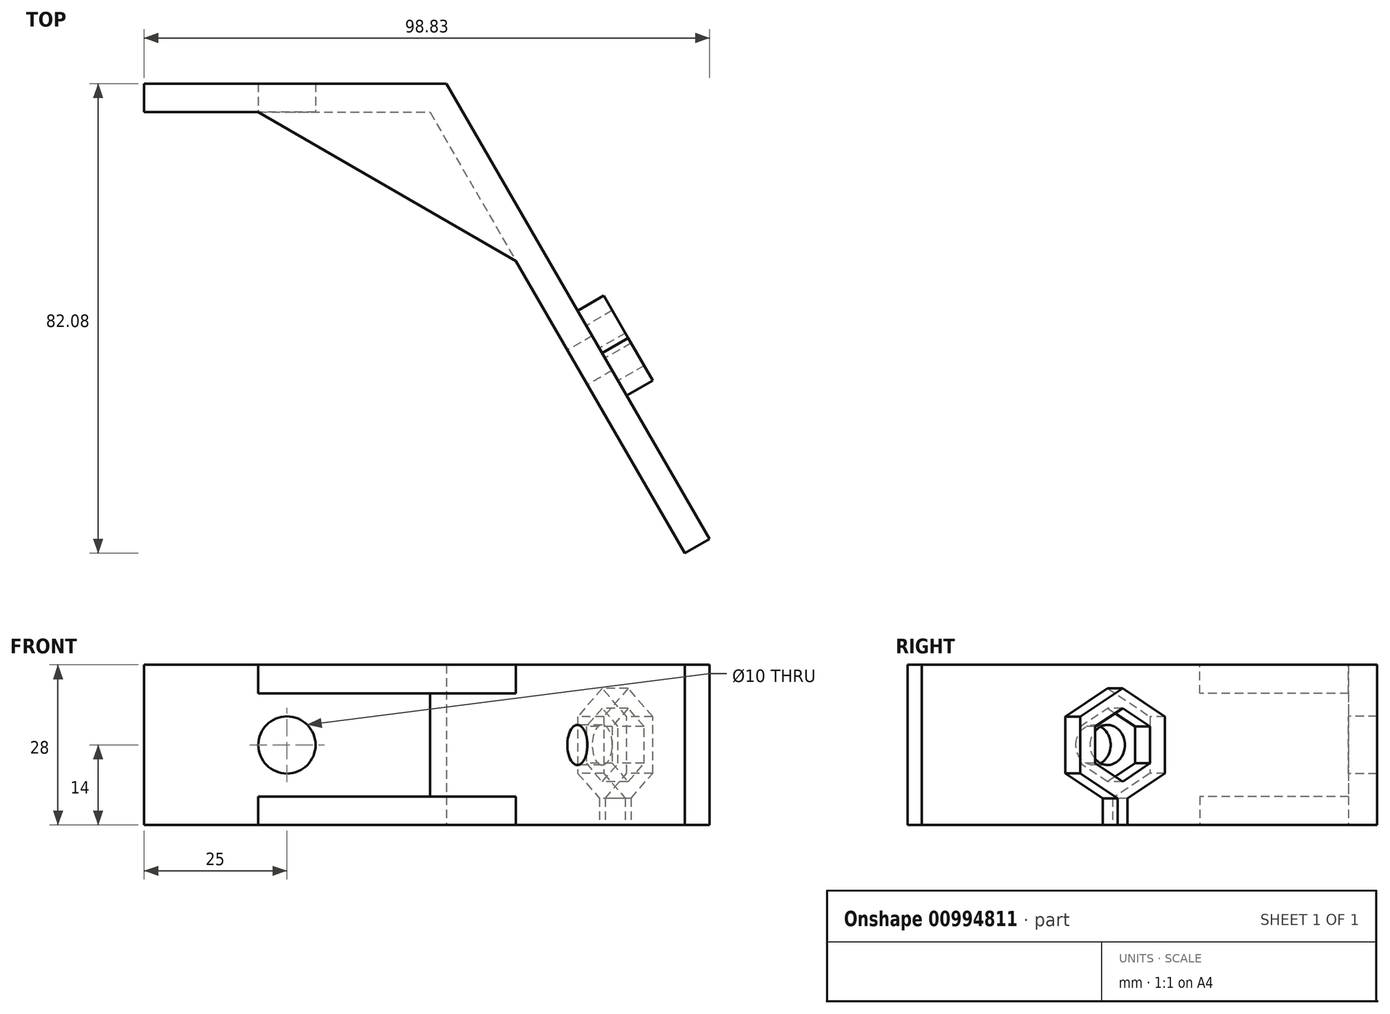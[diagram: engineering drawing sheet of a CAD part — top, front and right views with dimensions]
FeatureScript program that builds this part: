
annotation { "Feature Type Name" : "Feature", "Feature Type Description" : "" }
export const myFeature = defineFeature(function(context is Context, id is Id, definition is map)
    precondition{}
    {
        {
            var Q0;
            Q0=qCreatedBy(makeId("Top.planeOp"),FACE);
            var sketch = newSketch(context, id + "F0", { "sketchPlane" : qUnion([Q0])});
            skLineSegment(sketch, "E0", {"start": v(0, 5) * mm, "end": v(0, 0) * mm});
            skLineSegment(sketch, "E1", {"start": v(0, 0) * mm, "end": v(50, 0) * mm});
            skLineSegment(sketch, "E2", {"start": v(50, 0) * mm, "end": v(94.5, -77.08) * mm});
            skLineSegment(sketch, "E3", {"start": v(94.5, -77.08) * mm, "end": v(98.83, -74.58) * mm});
            skLineSegment(sketch, "E4", {"start": v(98.83, -74.58) * mm, "end": v(52.89, 5) * mm});
            skLineSegment(sketch, "E5", {"start": v(52.89, 5) * mm, "end": v(0, 5) * mm});
            skSolve(sketch);
        }
        {
            var Q0;
            Q0 = qSketchRegion(id + "F0", true);
            extrude(context, id + "F1", {"entities" : qUnion([Q0]), "depth" : 28 * mm, "offsetDistance" : 25 * mm});
        }
        {
            var Q0;
            Q0=makeQuery(id+"F1.opExtrude","SWEPT_FACE",FACE,{"disambiguationData":[OSD([sQuery(id+"F0.wireOp",EDGE,"E1")])]});
            var sketch = newSketch(context, id + "F2", { "sketchPlane" : qUnion([Q0])});
            skLineSegment(sketch, "E6", {"start": v(0, 0) * mm, "end": v(50, 28) * mm, "construction": true});
            skLineSegment(sketch, "E7", {"start": v(50, 0) * mm, "end": v(0, 28) * mm, "construction": true});
            skCircle(sketch, "E8", {"center": v(25, 14) * mm, "radius": 5 * mm});
            skSolve(sketch);
        }
        {
            var Q0;
            Q0 = qSketchRegion(id + "F2", true);
            extrude(context, id + "F3", {"entities" : qUnion([Q0]), "operationType" : NewBodyOperationType.REMOVE, "endBound" : BoundingType.THROUGH_ALL, "oppositeDirection" : true, "depth" : 25 * mm, "offsetDistance" : 25 * mm});
        }
        {
            var Q0;
            Q0=makeQuery(id+"F1.opExtrude","SWEPT_FACE",FACE,{"disambiguationData":[OSD([sQuery(id+"F0.wireOp",EDGE,"E2")])]});
            var sketch = newSketch(context, id + "F4", { "sketchPlane" : qUnion([Q0])});
            skCircle(sketch, "E9", {"center": v(76.5, 14) * mm, "radius": 3.5 * mm});
            skLineSegment(sketch, "E10", {"start": v(25, 14) * mm, "end": v(114, 14) * mm, "construction": true});
            skSolve(sketch);
        }
        {
            var Q0;
            Q0 = qSketchRegion(id + "F4", true);
            extrude(context, id + "F5", {"entities" : qUnion([Q0]), "operationType" : NewBodyOperationType.REMOVE, "endBound" : BoundingType.THROUGH_ALL, "oppositeDirection" : true, "depth" : 25 * mm, "offsetDistance" : 25 * mm});
        }
        {
            var Q0;
            Q0=qCreatedBy(makeId("Top.planeOp"),FACE);
            var sketch = newSketch(context, id + "F6", { "sketchPlane" : qUnion([Q0])});
            skLineSegment(sketch, "E11.0", {"start": v(20, 0) * mm, "end": v(50, 0) * mm});
            skLineSegment(sketch, "E11.1", {"start": v(50, 0) * mm, "end": v(65, -25.98) * mm});
            skLineSegment(sketch, "E12", {"start": v(20, 0) * mm, "end": v(65, -25.98) * mm});
            skPoint(sketch, "E13.orphan", {"position": v(94.5, -77.08) * mm});
            skPoint(sketch, "E14.orphan", {"position": v(0, 0) * mm});
            skSolve(sketch);
        }
        {
            var Q0;
            Q0 = qSketchRegion(id + "F6", true);
            extrude(context, id + "F7", {"entities" : qUnion([Q0]), "operationType" : NewBodyOperationType.ADD, "depth" : 5 * mm, "offsetDistance" : 25 * mm});
        }
        {
            var Q0;
            Q0=makeQuery(id+"F1.opExtrude","CAP_FACE",FACE,{"disambiguationData":[OSD([sQuery(id+"F0.wireOp",EDGE,"E0"),sQuery(id+"F0.wireOp",EDGE,"E1"),sQuery(id+"F0.wireOp",EDGE,"E2"),sQuery(id+"F0.wireOp",EDGE,"E3"),sQuery(id+"F0.wireOp",EDGE,"E4"),sQuery(id+"F0.wireOp",EDGE,"E5")])],"isStart":false});
            var sketch = newSketch(context, id + "F8", { "sketchPlane" : qUnion([Q0])});
            skLineSegment(sketch, "E15.0.0", {"start": v(50, 0) * mm, "end": v(20, 0) * mm});
            skLineSegment(sketch, "E15.0.1", {"start": v(20, 0) * mm, "end": v(65, -25.98) * mm});
            skLineSegment(sketch, "E15.0.2", {"start": v(65, -25.98) * mm, "end": v(50, 0) * mm});
            skSolve(sketch);
        }
        {
            var Q0;
            Q0 = qSketchRegion(id + "F8", true);
            extrude(context, id + "F9", {"entities" : qUnion([Q0]), "operationType" : NewBodyOperationType.ADD, "oppositeDirection" : true, "depth" : 5 * mm, "offsetDistance" : 25 * mm});
        }
        {
            var Q0;
            Q0=makeQuery(id+"F1.opExtrude","SWEPT_FACE",FACE,{"disambiguationData":[OSD([sQuery(id+"F0.wireOp",EDGE,"E4")])]});
            var sketch = newSketch(context, id + "F10", { "sketchPlane" : qUnion([Q0])});
            skCircle(sketch, "E16.0", {"center": v(-76.5, 14) * mm, "radius": 3.5 * mm, "construction": true});
            skCircle(sketch, "E17.cCircle", {"center": v(-76.5, 14) * mm, "radius": 5.56 * mm, "construction": true});
            skLineSegment(sketch, "E17.0", {"start": v(-70.94, 17.21) * mm, "end": v(-70.94, 10.79) * mm});
            skLineSegment(sketch, "E17.1", {"start": v(-70.94, 10.79) * mm, "end": v(-76.5, 7.58) * mm});
            skLineSegment(sketch, "E17.2", {"start": v(-76.5, 7.58) * mm, "end": v(-82.06, 10.79) * mm});
            skLineSegment(sketch, "E17.3", {"start": v(-82.06, 10.79) * mm, "end": v(-82.06, 17.21) * mm});
            skLineSegment(sketch, "E17.4", {"start": v(-82.06, 17.21) * mm, "end": v(-76.5, 20.42) * mm});
            skLineSegment(sketch, "E17.5", {"start": v(-76.5, 20.42) * mm, "end": v(-70.94, 17.21) * mm});
            skPoint(sketch, "E17.0.midPoint", {"position": v(-70.94, 14) * mm});
            skLineSegment(sketch, "E18.0", {"start": v(-85.06, 9.06) * mm, "end": v(-85.06, 18.94) * mm});
            skLineSegment(sketch, "E18.1", {"start": v(-76.5, 23.89) * mm, "end": v(-67.94, 18.94) * mm});
            skLineSegment(sketch, "E18.2", {"start": v(-67.94, 18.94) * mm, "end": v(-67.94, 9.06) * mm});
            skLineSegment(sketch, "E18.3", {"start": v(-85.06, 18.94) * mm, "end": v(-76.5, 23.89) * mm});
            skLineSegment(sketch, "E18.4", {"start": v(-67.94, 9.06) * mm, "end": v(-76.5, 4.11) * mm});
            skLineSegment(sketch, "E18.5", {"start": v(-76.5, 4.11) * mm, "end": v(-85.06, 9.06) * mm});
            skSolve(sketch);
        }
        {
            var Q0;
            Q0 = qSketchRegion(id + "F10", true);
            extrude(context, id + "F11", {"entities" : qUnion([Q0]), "operationType" : NewBodyOperationType.ADD, "depth" : 5.24 * mm, "offsetDistance" : 25 * mm});
        }
        {
            var Q0;
            {var subQ1=sQuery(id+"F0.wireOp",EDGE,"E4");var subQ2=sQuery(id+"F0.wireOp",EDGE,"E3");Q0=makeQuery(id+"F11.boolean.opBoolean","SPLIT",FACE,{"disambiguationData":[TD([makeQuery(id+"F1.opExtrude","SWEPT_FACE",FACE,{"disambiguationData":[OSD([subQ2])]})])],"derivedFrom":makeQuery(id+"F1.opExtrude","SWEPT_FACE",FACE,{"disambiguationData":[OSD([subQ1])]})});}
            var sketch = newSketch(context, id + "F12", { "sketchPlane" : qUnion([Q0])});
            skLineSegment(sketch, "E19.0", {"start": v(-67.94, 9.06) * mm, "end": v(-76.5, 4.11) * mm});
            skLineSegment(sketch, "E19.1", {"start": v(-76.5, 4.11) * mm, "end": v(-85.06, 9.06) * mm});
            skLineSegment(sketch, "E19.2", {"start": v(-114, 0) * mm, "end": v(-22.11, 0) * mm});
            skLineSegment(sketch, "E20", {"start": v(-76.5, 4.11) * mm, "end": v(-76.5, 0) * mm, "construction": true});
            skLineSegment(sketch, "E21", {"start": v(-77.5, 4.7) * mm, "end": v(-77.5, 0) * mm});
            skLineSegment(sketch, "E22", {"start": v(-75.5, 4.7) * mm, "end": v(-75.5, 0) * mm});
            skSolve(sketch);
        }
        {
            var Q0;
            Q0 = qSketchRegion(id + "F12", true);
            var Q1;
            Q1=makeQuery(id+"F11.opExtrude","CAP_FACE",FACE,{"disambiguationData":[OSD([sQuery(id+"F10.wireOp",EDGE,"E17.0"),sQuery(id+"F10.wireOp",EDGE,"E17.1"),sQuery(id+"F10.wireOp",EDGE,"E17.2"),sQuery(id+"F10.wireOp",EDGE,"E17.3"),sQuery(id+"F10.wireOp",EDGE,"E17.4"),sQuery(id+"F10.wireOp",EDGE,"E17.5"),sQuery(id+"F10.wireOp",EDGE,"E18.0"),sQuery(id+"F10.wireOp",EDGE,"E18.1"),sQuery(id+"F10.wireOp",EDGE,"E18.2"),sQuery(id+"F10.wireOp",EDGE,"E18.3"),sQuery(id+"F10.wireOp",EDGE,"E18.4"),sQuery(id+"F10.wireOp",EDGE,"E18.5")])],"isStart":false});
            extrude(context, id + "F13", {"entities" : qUnion([Q0]), "operationType" : NewBodyOperationType.ADD, "endBound" : BoundingType.UP_TO_SURFACE, "depth" : 25 * mm, "endBoundEntityFace" : qUnion([Q1]), "offsetDistance" : 25 * mm});
        }
    });
